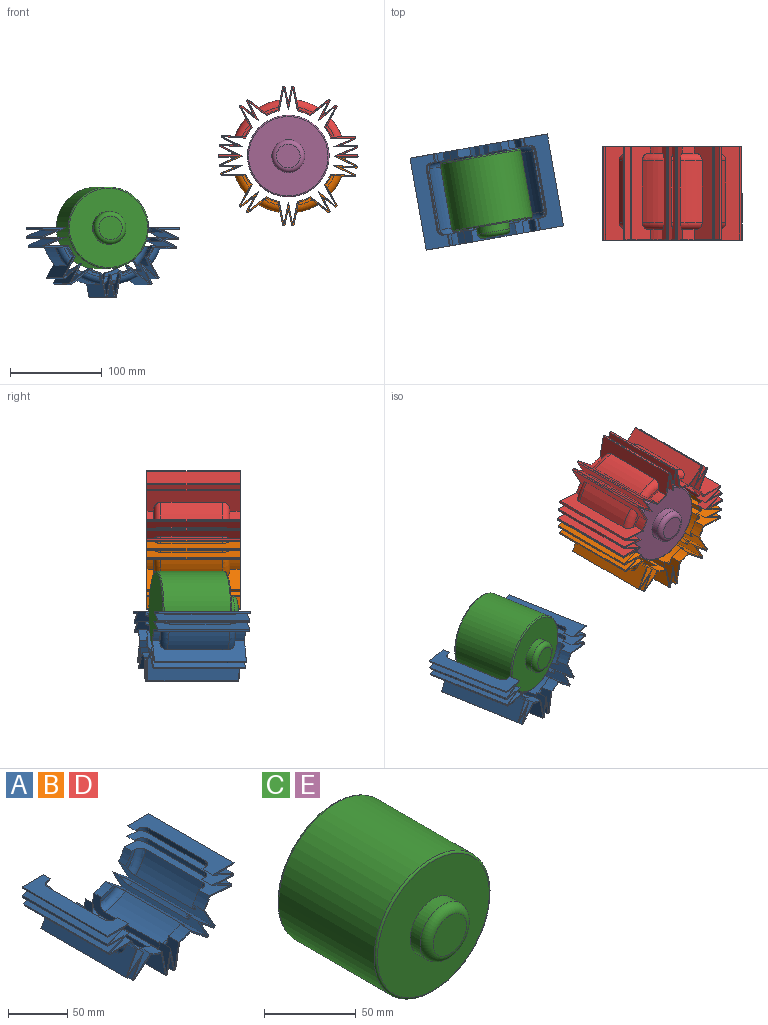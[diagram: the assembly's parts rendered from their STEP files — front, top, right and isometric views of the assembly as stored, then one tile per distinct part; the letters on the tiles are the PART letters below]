
ASSEMBLY  parts=5 mates=5
PART A: 172 faces, bbox 151.8x101.7x75.9 mm
  f0: cylinder r=75.89mm len=101.6mm, axis (0,1,0), area 231.6mm2, adj f21,f22,f128,f171
  f1: cylinder r=75.89mm len=101.6mm, axis (0,1,0), area 230.9mm2, adj f21,f22,f157,f159
  f2: cylinder r=75.89mm len=101.6mm, axis (0,1,0), area 230.9mm2, adj f21,f22,f144,f156
  f3: cylinder r=75.89mm len=101.6mm, axis (0,1,0), area 230.9mm2, adj f21,f22,f143,f145
  f4: cylinder r=75.89mm len=101.6mm, axis (0,1,0), area 230.9mm2, adj f21,f22,f130,f142
  f5: cylinder r=75.89mm len=101.6mm, axis (0,1,0), area 230.5mm2, adj f21,f22,f129,f131
  f6: cylinder r=75.89mm len=101.6mm, axis (0,1,0), area 129mm2, adj f12,f21,f22,f167
  f7: cylinder r=75.89mm len=101.6mm, axis (0,1,0), area 230.9mm2, adj f21,f22,f119,f120
  f8: cylinder r=75.89mm len=101.6mm, axis (0,1,0), area 129mm2, adj f21,f22,f53,f121
  f9: cylinder r=75.89mm len=101.6mm, axis (0,1,0), area 230.9mm2, adj f21,f22,f107,f118
  f10: cylinder r=75.89mm len=101.6mm, axis (0,1,0), area 230.9mm2, adj f21,f22,f105,f106
  f11: cylinder r=75.89mm len=101.6mm, axis (0,1,0), area 230.9mm2, adj f21,f22,f104,f158
  f12: plane 101.6x25.55mm, normal (0,0,1), area 1791.2mm2, adj f6,f21,f22,f28,f34,f40,f46,f52
  f13: cylinder r=50.26mm len=14.01mm, axis (0,1,0), area 133.1mm2, adj f22,f23,f72,f84
  f14: cylinder r=50.26mm len=11.75mm, axis (0,1,0), area 121.9mm2, adj f22,f24,f76,f85
  f15: cylinder r=50.26mm len=14.01mm, axis (0,1,0), area 133.1mm2, adj f22,f26,f68,f71
  f16: cylinder r=50.26mm len=11.71mm, axis (0,1,0), area 121.5mm2, adj f22,f27,f54,f67
  f17: cylinder r=50.26mm len=14.01mm, axis (0,1,0), area 190.1mm2, adj f21,f29,f72,f84
  f18: cylinder r=50.26mm len=12.7mm, axis (0,1,0), area 174.2mm2, adj f21,f30,f76,f85
  f19: cylinder r=50.26mm len=14.01mm, axis (0,1,0), area 190.1mm2, adj f21,f32,f68,f71
  f20: cylinder r=50.26mm len=12.7mm, axis (0,1,0), area 173.6mm2, adj f21,f33,f59,f67
  f21: plane 151.78x75.8mm, normal (0,-1,0), area 741.4mm2, adj f0,f1,f2,f3,f4,f5,f6,f7
  f22: plane 151.78x75.8mm, normal (0,1,0), area 741.4mm2, adj f0,f1,f2,f3,f4,f5,f6,f7
  f23: plane 18.22x9.33mm, normal (0,-1,0), area 69.1mm2, adj f13,f47,f72,f84
  f24: plane 15.54x11.3mm, normal (0,-1,0), area 63.8mm2, adj f14,f48,f76,f85
  f25: plane 3.93x1.63mm, normal (0,-1,0), area 3.2mm2, adj f49,f53,f75
  f26: plane 18.22x9.33mm, normal (0,-1,0), area 69.1mm2, adj f15,f50,f68,f71
  f27: plane 15.5x11.18mm, normal (0,-1,0), area 63.1mm2, adj f16,f51,f54,f55,f67
  f28: plane 3.93x1.91mm, normal (0,-1,0), area 3.8mm2, adj f12,f52,f58
  f29: plane 18.22x9.33mm, normal (0,1,0), area 69.1mm2, adj f17,f35,f72,f84
  f30: plane 15.54x11.3mm, normal (0,1,0), area 63.8mm2, adj f18,f36,f76,f85
  f31: plane 3.93x1.63mm, normal (0,1,0), area 3.2mm2, adj f37,f53,f75
  f32: plane 18.22x9.33mm, normal (0,1,0), area 69.1mm2, adj f19,f38,f68,f71
  f33: plane 15.5x11.18mm, normal (0,1,0), area 63.1mm2, adj f20,f39,f55,f59,f67
  f34: plane 3.93x1.91mm, normal (0,1,0), area 3.8mm2, adj f12,f40,f58
  f35: torus R=54.27mm, axis (0,-1,0), area 239.7mm2, adj f29,f41,f72,f84
  f36: torus R=54.27mm, axis (0,-1,0), area 225.2mm2, adj f30,f42,f76,f85
  f37: torus R=54.27mm, axis (0,-1,0), area 32.8mm2, adj f31,f43,f53,f75
  f38: torus R=54.27mm, axis (0,-1,0), area 239.7mm2, adj f32,f44,f68,f71
  f39: torus R=54.27mm, axis (0,-1,0), area 219.2mm2, adj f33,f45,f55,f67
  f40: torus R=54.27mm, axis (0,-1,0), area 38.4mm2, adj f12,f34,f46,f58
  f41: cylinder r=60.62mm len=67.31mm, axis (0,-1,0), area 1790.9mm2, adj f35,f47,f72,f84
  f42: cylinder r=60.62mm len=67.31mm, axis (0,-1,0), area 1689.1mm2, adj f36,f48,f76,f85
  f43: cylinder r=60.62mm len=67.31mm, axis (0,-1,0), area 285.1mm2, adj f37,f49,f53,f75
  f44: cylinder r=60.62mm len=67.31mm, axis (0,-1,0), area 1790.9mm2, adj f38,f50,f68,f71
  f45: cylinder r=60.62mm len=67.31mm, axis (0,-1,0), area 1638.8mm2, adj f39,f51,f55,f67
  f46: cylinder r=60.62mm len=67.31mm, axis (0,-1,0), area 333.5mm2, adj f12,f40,f52,f58
  f47: torus R=54.27mm, axis (0,-1,0), area 239.7mm2, adj f23,f41,f72,f84
  f48: torus R=54.27mm, axis (0,-1,0), area 225.2mm2, adj f24,f42,f76,f85
  f49: torus R=54.27mm, axis (0,-1,0), area 32.8mm2, adj f25,f43,f53,f75
  f50: torus R=54.27mm, axis (0,-1,0), area 239.7mm2, adj f26,f44,f68,f71
  f51: torus R=54.27mm, axis (0,-1,0), area 219.2mm2, adj f27,f45,f55,f67
  f52: torus R=54.27mm, axis (0,-1,0), area 38.4mm2, adj f12,f28,f46,f58
  f53: plane 101.6x25.55mm, normal (0,0,1), area 1791.2mm2, adj f8,f21,f22,f25,f31,f37,f43,f49
  f54: plane 8.89x0.09mm, normal (0.11,0,0.99), area 0.8mm2, adj f16,f22,f27,f55
  f55: plane 101.6x25.64mm, normal (0.06,0,1), area 1766.3mm2, adj f21,f22,f27,f33,f39,f45,f51,f54
  f56: plane 101.6x22.67mm, normal (-0.44,0,-0.9), area 1740.9mm2, adj f21,f22,f55,f57,f60,f61,f62,f63
  f57: plane 101.6x24.82mm, normal (0.06,0,1), area 1717.5mm2, adj f21,f22,f56,f58,f60,f61,f62,f63
  f58: plane 101.6x23.82mm, normal (-0.44,0,-0.9), area 1816.8mm2, adj f12,f21,f22,f28,f34,f40,f46,f52
  f59: plane 12.7x0.09mm, normal (0.11,0,0.99), area 1.1mm2, adj f20,f21,f33,f55
  f60: torus R=54.27mm, axis (0,-1,0), area 31.5mm2, adj f56,f57,f61,f64
  f61: cylinder r=60.62mm len=67.31mm, axis (0,-1,0), area 274.5mm2, adj f56,f57,f60,f62
  f62: torus R=54.27mm, axis (0,-1,0), area 31.5mm2, adj f56,f57,f61,f63
  f63: plane 3.93x1.78mm, normal (0,1,0), area 3mm2, adj f56,f57,f62
  f64: plane 3.93x1.78mm, normal (0,-1,0), area 3mm2, adj f56,f57,f60
  f65: plane 101.6x21.97mm, normal (-0.88,0,-0.48), area 1727.8mm2, adj f21,f22,f66,f68,f91,f92,f93,f94
  f66: plane 101.6x19.54mm, normal (0.63,0,0.78), area 1727.8mm2, adj f21,f22,f65,f67,f91,f92,f93,f94
  f67: plane 101.6x22.94mm, normal (-0.88,0,-0.48), area 1791.2mm2, adj f16,f20,f21,f22,f27,f33,f39,f45
  f68: plane 101.6x20.4mm, normal (0.63,0,0.78), area 1791.2mm2, adj f15,f19,f21,f22,f26,f32,f38,f44
  f69: plane 101.6x24.58mm, normal (-0.98,0,0.2), area 1727.8mm2, adj f21,f22,f70,f72,f96,f97,f98,f99
  f70: plane 101.6x24.58mm, normal (0.98,0,0.2), area 1727.8mm2, adj f21,f22,f69,f71,f96,f97,f98,f99
  f71: plane 101.6x25.66mm, normal (-0.98,0,0.2), area 1791.2mm2, adj f15,f19,f21,f22,f26,f32,f38,f44
  f72: plane 101.6x25.66mm, normal (0.98,0,0.2), area 1791.2mm2, adj f13,f17,f21,f22,f23,f29,f35,f41
  f73: plane 101.6x25.06mm, normal (0,0,1), area 1727.8mm2, adj f21,f22,f74,f75,f77,f78,f79,f80
  f74: plane 101.6x23.12mm, normal (0.39,0,-0.92), area 1727.8mm2, adj f21,f22,f73,f76,f77,f78,f79,f80
  f75: plane 101.6x24.06mm, normal (0.39,0,-0.92), area 1789.3mm2, adj f21,f22,f25,f31,f37,f43,f49,f53
  f76: plane 101.6x26.16mm, normal (0,0,1), area 1791.2mm2, adj f14,f18,f21,f22,f24,f30,f36,f42
  f77: torus R=54.27mm, axis (0,-1,0), area 31.5mm2, adj f73,f74,f78,f81
  f78: cylinder r=60.62mm len=67.31mm, axis (0,-1,0), area 274.3mm2, adj f73,f74,f77,f79
  f79: torus R=54.27mm, axis (0,-1,0), area 31.5mm2, adj f73,f74,f78,f80
  f80: plane 4x1.54mm, normal (0,1,0), area 3.1mm2, adj f73,f74,f79
  f81: plane 4x1.54mm, normal (0,-1,0), area 3.1mm2, adj f73,f74,f77
  f82: plane 101.6x19.54mm, normal (-0.63,0,0.78), area 1727.8mm2, adj f21,f22,f83,f85,f86,f87,f88,f89
  f83: plane 101.6x21.97mm, normal (0.88,0,-0.48), area 1727.8mm2, adj f21,f22,f82,f84,f86,f87,f88,f89
  f84: plane 101.6x20.4mm, normal (-0.63,0,0.78), area 1791.2mm2, adj f13,f17,f21,f22,f23,f29,f35,f41
  f85: plane 101.6x22.94mm, normal (0.88,0,-0.48), area 1791.2mm2, adj f14,f18,f21,f22,f24,f30,f36,f42
  f86: torus R=54.27mm, axis (0,-1,0), area 31.5mm2, adj f82,f83,f87,f90
  f87: cylinder r=60.62mm len=67.31mm, axis (0,-1,0), area 274.3mm2, adj f82,f83,f86,f88
  f88: torus R=54.27mm, axis (0,-1,0), area 31.5mm2, adj f82,f83,f87,f89
  f89: plane 3.5x3.12mm, normal (0,1,0), area 3.1mm2, adj f82,f83,f88
  f90: plane 3.5x3.12mm, normal (0,-1,0), area 3.1mm2, adj f82,f83,f86
  f91: torus R=54.27mm, axis (0,-1,0), area 31.5mm2, adj f65,f66,f92,f95
  f92: cylinder r=60.62mm len=67.31mm, axis (0,-1,0), area 274.3mm2, adj f65,f66,f91,f93
  f93: torus R=54.27mm, axis (0,-1,0), area 31.5mm2, adj f65,f66,f92,f94
  f94: plane 3.5x3.12mm, normal (0,1,0), area 3.1mm2, adj f65,f66,f93
  f95: plane 3.5x3.12mm, normal (0,-1,0), area 3.1mm2, adj f65,f66,f91
  f96: torus R=54.27mm, axis (0,-1,0), area 31.5mm2, adj f69,f70,f97,f100
  f97: cylinder r=60.62mm len=67.31mm, axis (0,-1,0), area 274.3mm2, adj f69,f70,f96,f98
  f98: torus R=54.27mm, axis (0,-1,0), area 31.5mm2, adj f69,f70,f97,f99
  f99: plane 3.93x1.56mm, normal (0,1,0), area 3.1mm2, adj f69,f70,f98
  f100: plane 3.93x1.56mm, normal (0,-1,0), area 3.1mm2, adj f69,f70,f96
  f101: torus R=54.27mm, axis (0,-1,0), area 12.1mm2, adj f102,f104,f105
  f102: cylinder r=61.89mm len=67.31mm, axis (0,-1,0), area 134.6mm2, adj f101,f103,f104,f105
  f103: torus R=54.27mm, axis (0,-1,0), area 12.1mm2, adj f102,f104,f105
  f104: plane 101.6x16.94mm, normal (-0.88,0,0.48), area 1564.2mm2, adj f11,f21,f22,f101,f102,f103,f105
  f105: plane 101.6x15.07mm, normal (0.63,0,-0.78), area 1564.2mm2, adj f10,f21,f22,f101,f102,f103,f104
  f106: plane 101.6x22.64mm, normal (-0.88,0,0.48), area 1731.2mm2, adj f10,f21,f22,f108,f109,f110,f111,f112
  f107: plane 101.6x25.82mm, normal (0,0,-1), area 1731.2mm2, adj f9,f21,f22,f108,f109,f110,f111,f112
  f108: torus R=54.27mm, axis (0,-1,0), area 248.4mm2, adj f106,f107,f109,f112
  f109: cylinder r=61.89mm len=67.31mm, axis (0,-1,0), area 1601.5mm2, adj f106,f107,f108,f110
  f110: torus R=54.27mm, axis (0,-1,0), area 248.4mm2, adj f106,f107,f109,f111
  f111: plane 13.21x9.27mm, normal (0,-1,0), area 38mm2, adj f106,f107,f110,f113
  f112: plane 13.21x9.27mm, normal (0,1,0), area 38mm2, adj f106,f107,f108,f114
  f113: cylinder r=51.53mm len=11.43mm, axis (0,1,0), area 141.3mm2, adj f21,f106,f107,f111
  f114: cylinder r=51.53mm len=10.61mm, axis (0,1,0), area 94.2mm2, adj f22,f106,f107,f112
  f115: torus R=54.27mm, axis (0,-1,0), area 12.1mm2, adj f116,f118,f119
  f116: cylinder r=61.89mm len=67.31mm, axis (0,-1,0), area 134.6mm2, adj f115,f117,f118,f119
  f117: torus R=54.27mm, axis (0,-1,0), area 12.1mm2, adj f116,f118,f119
  f118: plane 101.6x17.83mm, normal (-0.39,0,0.92), area 1564.2mm2, adj f9,f21,f22,f115,f116,f117,f119
  f119: plane 101.6x19.32mm, normal (0,0,-1), area 1564.2mm2, adj f7,f21,f22,f115,f116,f117,f118
  f120: plane 101.6x18.68mm, normal (-0.39,0,0.92), area 1624.2mm2, adj f7,f21,f22,f121,f122,f123,f124
  f121: plane 101.66x19.27mm, normal (0,0,-1), area 1546.6mm2, adj f8,f21,f22,f120,f122,f123,f124
  f122: torus R=54.27mm, axis (0,-1,0), area 13mm2, adj f120,f121,f123
  f123: cylinder r=61.89mm len=67.31mm, axis (0,-1,0), area 144.1mm2, adj f120,f121,f122,f124
  f124: torus R=54.27mm, axis (0,-1,0), area 13mm2, adj f120,f121,f123
  f125: torus R=54.27mm, axis (0,-1,0), area 12.1mm2, adj f126,f128,f129
  f126: cylinder r=61.89mm len=67.31mm, axis (0,-1,0), area 134.7mm2, adj f125,f127,f128,f129
  f127: torus R=54.27mm, axis (0,-1,0), area 12.1mm2, adj f126,f128,f129
  f128: plane 101.6x19.15mm, normal (-0.06,0,-1), area 1554.3mm2, adj f0,f21,f22,f125,f126,f127,f129
  f129: plane 101.6x17.49mm, normal (0.44,0,0.9), area 1576.7mm2, adj f5,f21,f22,f125,f126,f127,f128
  f130: plane 101.6x22.64mm, normal (0.88,0,0.48), area 1731.2mm2, adj f4,f21,f22,f132,f133,f134,f135,f136
  f131: plane 101.6x25.38mm, normal (-0.06,0,-1), area 1708.1mm2, adj f5,f21,f22,f132,f133,f134,f135,f136
  f132: torus R=54.27mm, axis (0,-1,0), area 240.9mm2, adj f130,f131,f133,f136
  f133: cylinder r=61.89mm len=67.31mm, axis (0,-1,0), area 1546.9mm2, adj f130,f131,f132,f134
  f134: torus R=54.27mm, axis (0,-1,0), area 240.9mm2, adj f130,f131,f133,f135
  f135: plane 13.11x9.16mm, normal (0,-1,0), area 37.5mm2, adj f130,f131,f134,f137
  f136: plane 13.11x9.16mm, normal (0,1,0), area 37.5mm2, adj f130,f131,f132,f138
  f137: cylinder r=51.53mm len=11.43mm, axis (0,1,0), area 140.1mm2, adj f21,f130,f131,f135
  f138: cylinder r=51.53mm len=10.51mm, axis (0,1,0), area 93.4mm2, adj f22,f130,f131,f136
  f139: torus R=54.27mm, axis (0,-1,0), area 12.1mm2, adj f140,f142,f143
  f140: cylinder r=61.89mm len=67.31mm, axis (0,-1,0), area 134.6mm2, adj f139,f141,f142,f143
  f141: torus R=54.27mm, axis (0,-1,0), area 12.1mm2, adj f140,f142,f143
  f142: plane 101.6x15.07mm, normal (-0.63,0,-0.78), area 1564.2mm2, adj f4,f21,f22,f139,f140,f141,f143
  f143: plane 101.6x16.94mm, normal (0.88,0,0.48), area 1564.2mm2, adj f3,f21,f22,f139,f140,f141,f142
  f144: plane 101.6x25.33mm, normal (0.98,0,-0.2), area 1731.2mm2, adj f2,f21,f22,f146,f147,f148,f149,f150
  f145: plane 101.6x20.14mm, normal (-0.63,0,-0.78), area 1731.2mm2, adj f3,f21,f22,f146,f147,f148,f149,f150
  f146: torus R=54.27mm, axis (0,-1,0), area 266.1mm2, adj f144,f145,f147,f150
  f147: cylinder r=61.89mm len=67.31mm, axis (0,-1,0), area 1705.4mm2, adj f144,f145,f146,f148
  f148: torus R=54.27mm, axis (0,-1,0), area 266.1mm2, adj f144,f145,f147,f149
  f149: plane 15.69x7.57mm, normal (0,-1,0), area 41.6mm2, adj f144,f145,f148,f151
  f150: plane 15.69x7.57mm, normal (0,1,0), area 41.6mm2, adj f144,f145,f146,f152
  f151: cylinder r=51.53mm len=12.79mm, axis (0,1,0), area 156mm2, adj f21,f144,f145,f149
  f152: cylinder r=51.53mm len=12.79mm, axis (0,1,0), area 104mm2, adj f22,f144,f145,f150
  f153: torus R=54.27mm, axis (0,-1,0), area 12.1mm2, adj f154,f156,f157
  f154: cylinder r=61.89mm len=67.31mm, axis (0,-1,0), area 134.6mm2, adj f153,f155,f156,f157
  f155: torus R=54.27mm, axis (0,-1,0), area 12.1mm2, adj f154,f156,f157
  f156: plane 101.6x18.95mm, normal (-0.98,0,-0.2), area 1564.2mm2, adj f2,f21,f22,f153,f154,f155,f157
  f157: plane 101.6x18.95mm, normal (0.98,0,-0.2), area 1564.2mm2, adj f1,f21,f22,f153,f154,f155,f156
  f158: plane 101.6x20.14mm, normal (0.63,0,-0.78), area 1731.2mm2, adj f11,f21,f22,f160,f161,f162,f163,f164
  f159: plane 101.6x25.33mm, normal (-0.98,0,-0.2), area 1731.2mm2, adj f1,f21,f22,f160,f161,f162,f163,f164
  f160: torus R=54.27mm, axis (0,-1,0), area 266.1mm2, adj f158,f159,f161,f164
  f161: cylinder r=61.89mm len=67.31mm, axis (0,-1,0), area 1705.4mm2, adj f158,f159,f160,f162
  f162: torus R=54.27mm, axis (0,-1,0), area 266.1mm2, adj f158,f159,f161,f163
  f163: plane 15.69x7.57mm, normal (0,-1,0), area 41.6mm2, adj f158,f159,f162,f165
  f164: plane 15.69x7.57mm, normal (0,1,0), area 41.6mm2, adj f158,f159,f160,f166
  f165: cylinder r=51.53mm len=12.79mm, axis (0,1,0), area 156mm2, adj f21,f158,f159,f163
  f166: cylinder r=51.53mm len=12.79mm, axis (0,1,0), area 104mm2, adj f22,f158,f159,f164
  f167: plane 101.67x20.15mm, normal (0,0,-1), area 1563.6mm2, adj f6,f21,f22,f168,f169,f170,f171
  f168: torus R=54.27mm, axis (0,-1,0), area 19.4mm2, adj f167,f169,f171
  f169: cylinder r=61.89mm len=67.31mm, axis (0,-1,0), area 196.6mm2, adj f167,f168,f170,f171
  f170: torus R=54.27mm, axis (0,-1,0), area 19.4mm2, adj f167,f169,f171
  f171: plane 101.6x19.32mm, normal (0.44,0,0.9), area 1667.6mm2, adj f0,f21,f22,f167,f168,f169,f170
PART B: same geometry as A
PART C: 8 faces, bbox 96.2x88.9x96.2 mm
  f0: cylinder r=44.45mm len=88.9mm, axis (0,1,0), area 20572.3mm2, adj f6,f7
  f1: plane 86.36x86.36mm, normal (0,-1,0), area 4851.2mm2, adj f3,f7
  f2: plane 86.36x86.36mm, normal (0,1,0), area 5857.5mm2, adj f6
  f3: cylinder r=17.9mm len=35.8mm, axis (0,1,0), area 856.9mm2, adj f1,f5
  f4: plane 25.64x25.64mm, normal (0,-1,0), area 516.2mm2, adj f5
  f5: torus R=12.82mm, axis (0,-1,0), area 804.8mm2, adj f3,f4
  f6: torus R=43.18mm, axis (0,-1,0), area 551.4mm2, adj f0,f2
  f7: torus R=43.18mm, axis (0,-1,0), area 551.4mm2, adj f0,f1
PART D: same geometry as A
PART E: same geometry as C
PLACE A rot(axis=(0,0,1),10deg) t=(51.94,51.07,98.87)mm
PLACE B rot(axis=(-0.08,-0.13,-0.99),0deg) t=(253.95,49.41,176.93)mm
PLACE C rot(axis=(0,0,1),10deg) t=(-87.73,28.38,98.87)mm
PLACE D rot(axis=(0,-1,0),180deg) t=(253.95,49.41,176.93)mm
PLACE E t=(112.47,51.32,176.93)mm
MATE planar B.f0 <-> D.f0  axis (0,1,0) through (253.95,49.41,176.93)mm
MATE revolute D.f35 <-> E.f0  axis (0,-1,0) through (253.95,51.32,176.93)mm
MATE revolute C.f0 <-> A.f35  axis (-0.17,0.98,0) through (51.6,52.95,98.87)mm
MATE revolute B.f35 <-> E.f0  axis (0,-1,0) through (253.95,51.32,176.93)mm
MATE planar A.f23 <-> C.f0  axis (0.17,-0.98,0) through (27.11,89.25,49.9)mm
